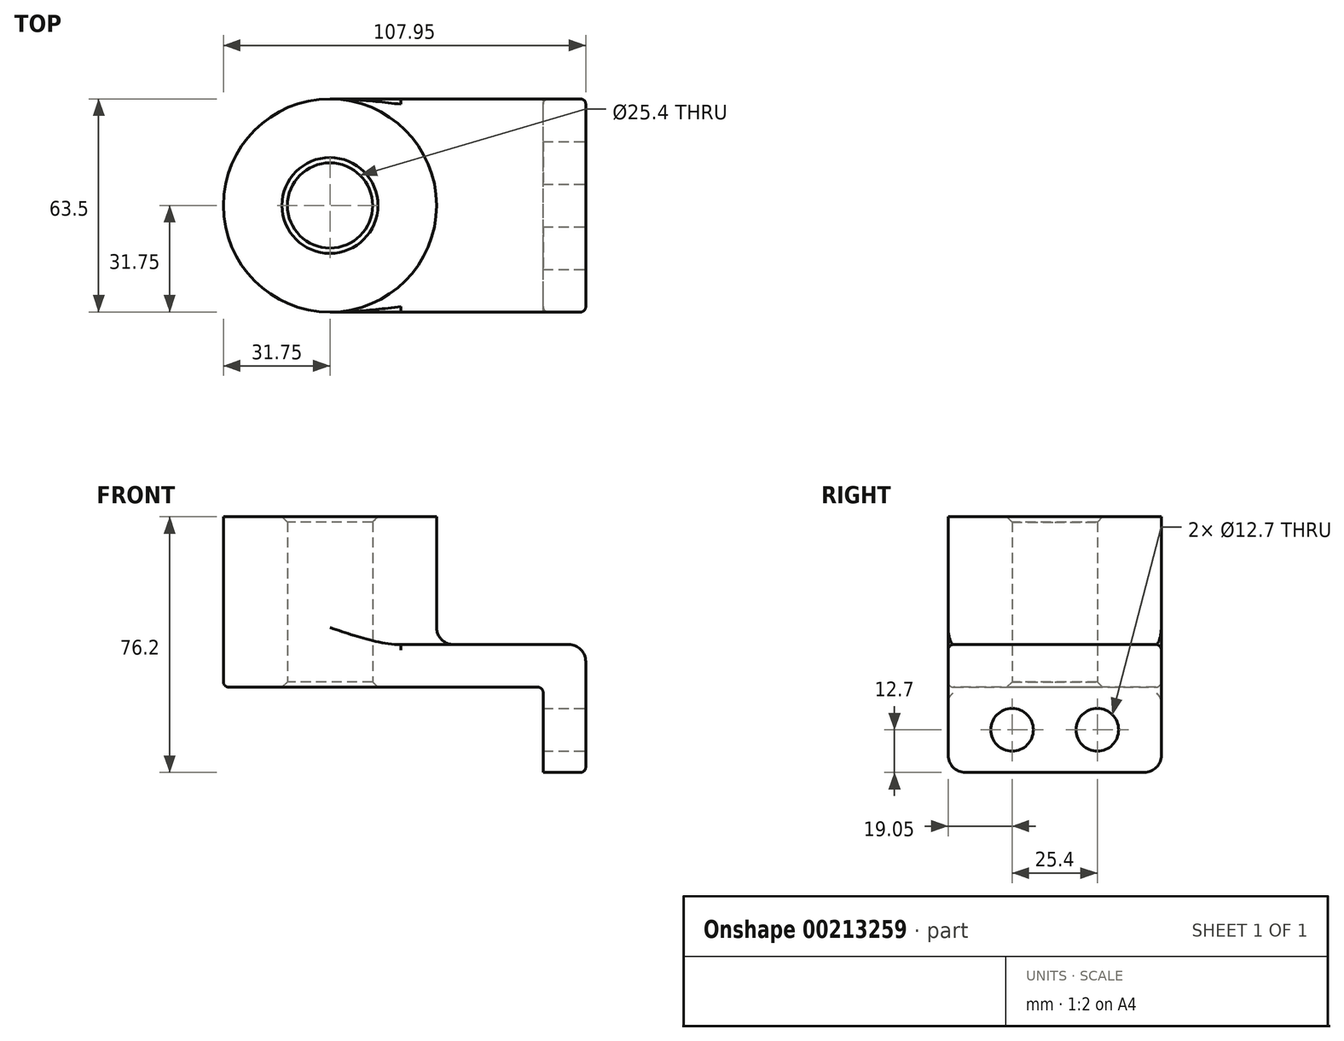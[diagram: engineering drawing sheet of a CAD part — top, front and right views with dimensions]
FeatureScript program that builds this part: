
annotation { "Feature Type Name" : "Feature", "Feature Type Description" : "" }
export const myFeature = defineFeature(function(context is Context, id is Id, definition is map)
    precondition{}
    {
        {
            var Q0;
            Q0=qCreatedBy(makeId("Top.planeOp"),FACE);
            var sketch = newSketch(context, id + "F0", { "sketchPlane" : qUnion([Q0])});
            skLineSegment(sketch, "E0.bottom", {"start": v(-38.1, 31.75) * mm, "end": v(38.1, 31.75) * mm});
            skLineSegment(sketch, "E0.top", {"start": v(-38.1, -31.75) * mm, "end": v(38.1, -31.75) * mm});
            skLineSegment(sketch, "E0.left", {"start": v(-38.1, 31.75) * mm, "end": v(-38.1, -31.75) * mm});
            skLineSegment(sketch, "E0.right", {"start": v(38.1, 31.75) * mm, "end": v(38.1, -31.75) * mm});
            skPoint(sketch, "E0.middle", {"position": v(0, 0) * mm});
            skCircle(sketch, "E1", {"center": v(-38.1, 0) * mm, "radius": 31.75 * mm});
            skCircle(sketch, "E2", {"center": v(-38.1, 0) * mm, "radius": 12.7 * mm});
            skSolve(sketch);
        }
        {
            var Q0;
            Q0 = qSketchRegion(id + "F0", true);
            extrude(context, id + "F1", {"entities" : qUnion([Q0]), "depth" : 12.7 * mm});
        }
        {
            var Q0;
            {var subQ1=sQuery(id+"F0.wireOp",EDGE,"E0.left");var subQ3=sQuery(id+"F0.wireOp",EDGE,"E2");var subQ4=makeQuery(id+"F0.imprint","INTERSECT",VERTEX,{"disambiguationData":[OD(0.0)],"derivedFrom":[subQ1,subQ3]});Q0=makeQuery(id+"F0.imprint","IMPRINT",FACE,{"disambiguationData":[TD([[makeQuery(id+"F0.imprint","IMPRINT",EDGE,{"disambiguationData":[TD([[subQ4,-1.0]])],"derivedFrom":subQ3}),-1.0]])]});}
            var Q1;
            {var subQ1=sQuery(id+"F0.wireOp",EDGE,"E0.left");var subQ3=sQuery(id+"F0.wireOp",EDGE,"E2");var subQ4=makeQuery(id+"F0.imprint","INTERSECT",VERTEX,{"disambiguationData":[OD(0.0)],"derivedFrom":[subQ1,subQ3]});Q1=makeQuery(id+"F0.imprint","IMPRINT",FACE,{"disambiguationData":[TD([[makeQuery(id+"F0.imprint","IMPRINT",EDGE,{"disambiguationData":[TD([[subQ4,1.0]])],"derivedFrom":subQ3}),-1.0]])]});}
            extrude(context, id + "F2", {"entities" : qUnion([Q0, Q1]), "operationType" : NewBodyOperationType.ADD, "depth" : 50.8 * mm});
        }
        {
            var Q0;
            Q0=makeQuery(id+"F1.opExtrude","SWEPT_FACE",FACE,{"disambiguationData":[OSD([sQuery(id+"F0.wireOp",EDGE,"E0.right")])]});
            var sketch = newSketch(context, id + "F3", { "sketchPlane" : qUnion([Q0])});
            skPoint(sketch, "E3.oppositeSnap0", {"position": v(31.75, 6.35) * mm});
            skLineSegment(sketch, "E3.bottom", {"start": v(-31.75, 12.7) * mm, "end": v(31.75, 12.7) * mm});
            skLineSegment(sketch, "E3.top", {"start": v(-31.75, -25.4) * mm, "end": v(31.75, -25.4) * mm});
            skLineSegment(sketch, "E3.left", {"start": v(-31.75, 12.7) * mm, "end": v(-31.75, -25.4) * mm});
            skLineSegment(sketch, "E3.right", {"start": v(31.75, 12.7) * mm, "end": v(31.75, -25.4) * mm});
            skCircle(sketch, "E4", {"center": v(-12.7, -12.7) * mm, "radius": 6.35 * mm});
            skLineSegment(sketch, "E5", {"start": v(0, 0) * mm, "end": v(0, -25.4) * mm, "construction": true});
            skCircle(sketch, "E6.MirrorC", {"center": v(12.7, -12.7) * mm, "radius": 6.35 * mm});
            skSolve(sketch);
        }
        {
            var Q0;
            Q0 = qSketchRegion(id + "F3", true);
            extrude(context, id + "F4", {"entities" : qUnion([Q0]), "operationType" : NewBodyOperationType.ADD, "oppositeDirection" : true, "depth" : 12.7 * mm});
        }
        {
            var Q0;
            {var subQ0=sQuery(id+"F0.wireOp",EDGE,"E1");Q0=makeQuery(id+"F2.boolean.opBoolean","INTERSECT",EDGE,{"derivedFrom":[makeQuery(id+"F1.opExtrude","CAP_FACE",FACE,{"disambiguationData":[OSD([sQuery(id+"F0.wireOp",EDGE,"E0.bottom"),sQuery(id+"F0.wireOp",EDGE,"E0.top"),sQuery(id+"F0.wireOp",EDGE,"E0.right"),subQ0,sQuery(id+"F0.wireOp",EDGE,"E2")])],"isStart":false}),makeQuery(id+"F2.opExtrude","SWEPT_FACE",FACE,{"disambiguationData":[OSD([subQ0])]})]});}
            var Q1;
            Q1=makeQuery(id+"F1.opExtrude","CAP_EDGE",EDGE,{"disambiguationData":[OSD([sQuery(id+"F0.wireOp",EDGE,"E0.right")])],"isStart":false});
            var Q2;
            Q2=makeQuery(id+"F4.opExtrude","SWEPT_EDGE",EDGE,{"disambiguationData":[OSD([sQuery(id+"F3.wireOp",EDGE,"E3.top"),sQuery(id+"F3.wireOp",EDGE,"E3.left")])]});
            var Q3;
            Q3=makeQuery(id+"F4.opExtrude","SWEPT_EDGE",EDGE,{"disambiguationData":[OSD([sQuery(id+"F3.wireOp",EDGE,"E3.top"),sQuery(id+"F3.wireOp",EDGE,"E3.right")])]});
            fillet(context, id + "F5", {"entities" : qUnion([Q0, Q1, Q2, Q3]), "radius" : 5.08 * mm, "tangentPropagation" : true, "allowEdgeOverflow" : false});
        }
        {
            var Q0;
            Q0=makeQuery(id+"F1.opExtrude","CAP_EDGE",EDGE,{"disambiguationData":[OSD([sQuery(id+"F0.wireOp",EDGE,"E0.top")])],"isStart":false});
            var Q1;
            Q1=makeQuery(id+"F1.opExtrude","CAP_EDGE",EDGE,{"disambiguationData":[OSD([sQuery(id+"F0.wireOp",EDGE,"E0.top")])],"isStart":true});
            var Q2;
            Q2=makeQuery(id+"F4.boolean.opBoolean","INTERSECT",EDGE,{"derivedFrom":[makeQuery(id+"F1.opExtrude","CAP_FACE",FACE,{"disambiguationData":[OSD([sQuery(id+"F0.wireOp",EDGE,"E0.bottom"),sQuery(id+"F0.wireOp",EDGE,"E0.top"),sQuery(id+"F0.wireOp",EDGE,"E0.right"),sQuery(id+"F0.wireOp",EDGE,"E1"),sQuery(id+"F0.wireOp",EDGE,"E2")])],"isStart":true}),makeQuery(id+"F4.opExtrude","CAP_FACE",FACE,{"disambiguationData":[OSD([sQuery(id+"F3.wireOp",EDGE,"E3.bottom"),sQuery(id+"F3.wireOp",EDGE,"E3.top"),sQuery(id+"F3.wireOp",EDGE,"E3.left"),sQuery(id+"F3.wireOp",EDGE,"E3.right"),sQuery(id+"F3.wireOp",EDGE,"E4"),sQuery(id+"F3.wireOp",EDGE,"E6.MirrorC")])],"isStart":false})]});
            fillet(context, id + "F6", {"entities" : qUnion([Q0, Q1, Q2]), "radius" : 1.59 * mm, "tangentPropagation" : true, "allowEdgeOverflow" : false});
        }
        {
            var Q0;
            {var subQ0=sQuery(id+"F0.wireOp",EDGE,"E2");Q0=makeQuery(id+"F2.boolean.opBoolean","MERGE",FACE,{"derivedFrom":[makeQuery(id+"F1.opExtrude","SWEPT_FACE",FACE,{"disambiguationData":[OSD([subQ0])]}),makeQuery(id+"F2.opExtrude","SWEPT_FACE",FACE,{"disambiguationData":[OSD([subQ0])]})]});}
            chamfer(context, id + "F7", {"entities" : qUnion([Q0]), "width" : 1.59 * mm, "tangentPropagation" : true});
        }
    });
